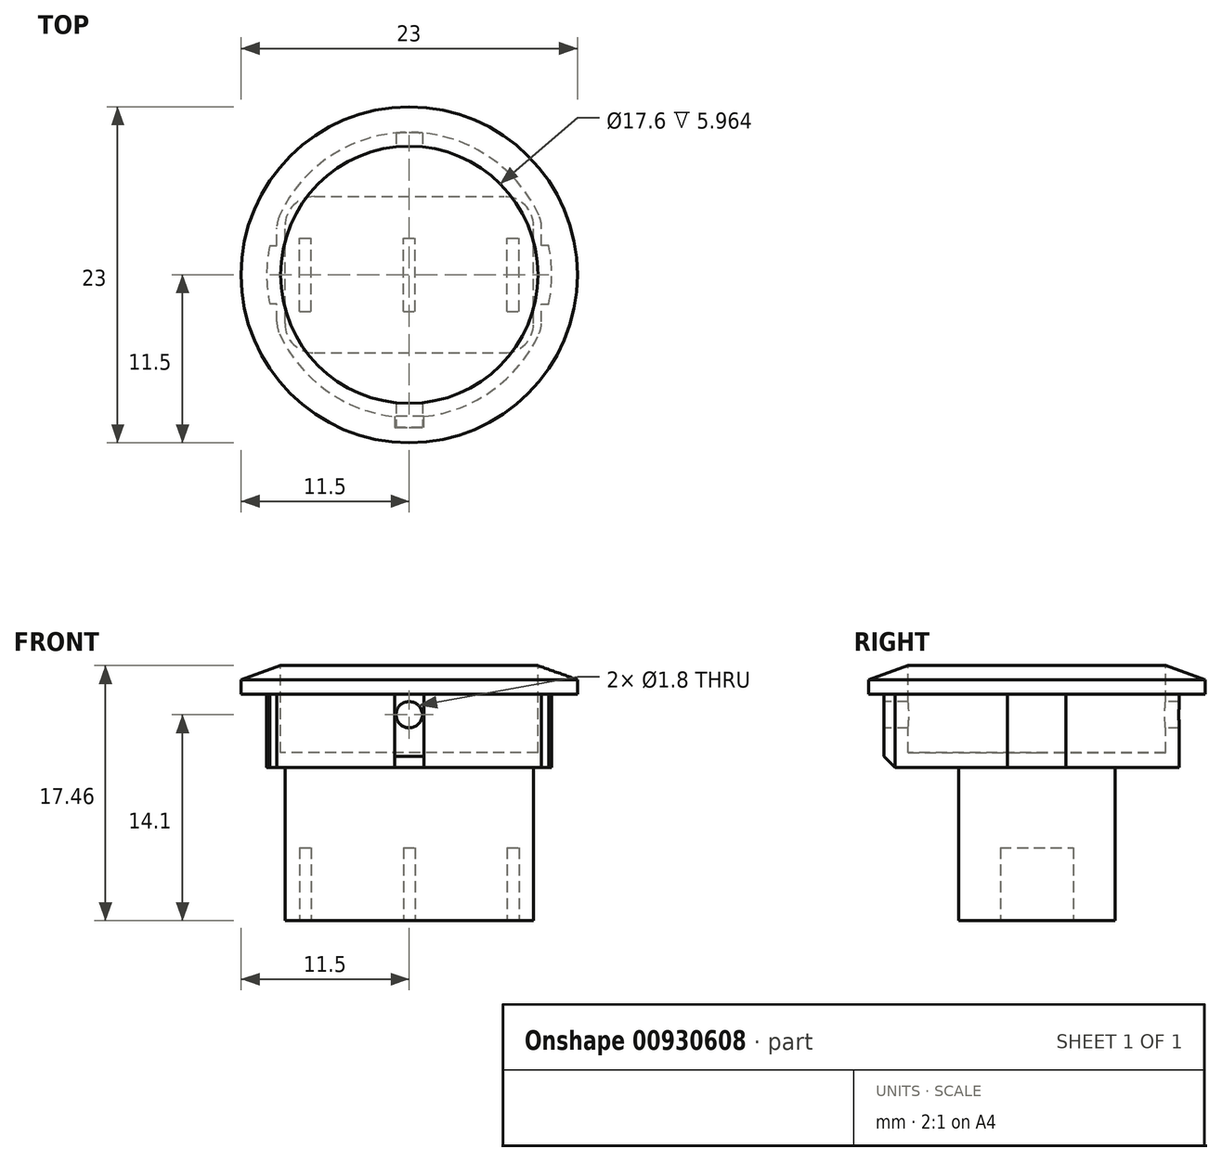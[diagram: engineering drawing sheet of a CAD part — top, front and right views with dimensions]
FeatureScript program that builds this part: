
annotation { "Feature Type Name" : "Feature", "Feature Type Description" : "" }
export const myFeature = defineFeature(function(context is Context, id is Id, definition is map)
    precondition{}
    {
        {
            var Q0;
            Q0=qCreatedBy(makeId("Top.planeOp"),FACE);
            var sketch = newSketch(context, id + "F0", { "sketchPlane" : qUnion([Q0])});
            skCircle(sketch, "E0", {"center": v(0, 0) * mm, "radius": 11.5 * mm});
            skSolve(sketch);
        }
        {
            var Q0;
            Q0=qSketchRegion(id+"F0",true);
            extrude(context, id + "F1", {"entities" : qUnion([Q0]), "depth" : 2 * mm, "offsetDistance" : 25 * mm});
        }
        {
            var Q0;
            Q0=makeQuery(id+"F1.opExtrude","CAP_FACE",FACE,{"disambiguationData":[OSD([sQuery(id+"F0.wireOp",EDGE,"E0")])],"isStart":true});
            var sketch = newSketch(context, id + "F2", { "sketchPlane" : qUnion([Q0])});
            skArc(sketch, "E1", {"start": v(-9.05, -3.63) * mm, "mid": v(0, -9.75) * mm, "end": v(9.05, -3.63) * mm});
            skLineSegment(sketch, "E2", {"start": v(-9.05, 3.63) * mm, "end": v(-9.05, -3.63) * mm});
            skLineSegment(sketch, "E3", {"start": v(9.05, 3.63) * mm, "end": v(9.05, -3.63) * mm});
            skArc(sketch, "E4.trimOffspring", {"start": v(9.05, 3.63) * mm, "mid": v(5.87, 7.78) * mm, "end": v(1, 9.7) * mm});
            skLineSegment(sketch, "E5", {"start": v(-1, 9.7) * mm, "end": v(-1, 10.45) * mm});
            skLineSegment(sketch, "E6", {"start": v(-1, 10.45) * mm, "end": v(1, 10.45) * mm});
            skLineSegment(sketch, "E7", {"start": v(1, 10.45) * mm, "end": v(1, 9.7) * mm});
            skArc(sketch, "E8.trimOffspring", {"start": v(-1, 9.7) * mm, "mid": v(-5.87, 7.78) * mm, "end": v(-9.05, 3.63) * mm});
            skLineSegment(sketch, "E9", {"start": v(-9.05, 2) * mm, "end": v(-9.54, 2) * mm});
            skLineSegment(sketch, "E10", {"start": v(-9.54, -2) * mm, "end": v(-9.05, -2) * mm});
            skLineSegment(sketch, "E11", {"start": v(9.05, 2) * mm, "end": v(9.54, 2) * mm});
            skLineSegment(sketch, "E12", {"start": v(9.54, -2) * mm, "end": v(9.05, -2) * mm});
            skArc(sketch, "E13", {"start": v(-9.05, 3.63) * mm, "mid": v(-9.33, 2.82) * mm, "end": v(-9.54, 2) * mm, "construction": true});
            skArc(sketch, "E14", {"start": v(9.05, -3.63) * mm, "mid": v(9.33, -2.82) * mm, "end": v(9.54, -2) * mm, "construction": true});
            skArc(sketch, "E15.trimOffspring", {"start": v(-9.54, -2) * mm, "mid": v(-9.33, -2.82) * mm, "end": v(-9.05, -3.63) * mm, "construction": true});
            skArc(sketch, "E16", {"start": v(-9.54, 2) * mm, "mid": v(-9.75, 0) * mm, "end": v(-9.54, -2) * mm});
            skArc(sketch, "E17.trimOffspring", {"start": v(9.54, 2) * mm, "mid": v(9.33, 2.82) * mm, "end": v(9.05, 3.63) * mm, "construction": true});
            skArc(sketch, "E18", {"start": v(9.54, -2) * mm, "mid": v(9.75, 0) * mm, "end": v(9.54, 2) * mm});
            skSolve(sketch);
        }
        {
            var Q0;
            Q0=qSketchRegion(id+"F2",true);
            extrude(context, id + "F3", {"entities" : qUnion([Q0]), "operationType" : NewBodyOperationType.ADD, "depth" : 5 * mm, "offsetDistance" : 25 * mm});
        }
        {
            var Q0;
            Q0=makeQuery(id+"F3.opExtrude","CAP_FACE",FACE,{"disambiguationData":[OSD([sQuery(id+"F2.wireOp",EDGE,"E1")])],"isStart":false});
            var sketch = newSketch(context, id + "F4", { "sketchPlane" : qUnion([Q0])});
            skLineSegment(sketch, "E19.bottom", {"start": v(-6.5, 5.35) * mm, "end": v(6.5, 5.35) * mm});
            skLineSegment(sketch, "E19.top", {"start": v(-6.5, -5.35) * mm, "end": v(6.5, -5.35) * mm});
            skLineSegment(sketch, "E19.left", {"start": v(-8.5, 3.35) * mm, "end": v(-8.5, -3.35) * mm});
            skLineSegment(sketch, "E19.right", {"start": v(8.5, 3.35) * mm, "end": v(8.5, -3.35) * mm});
            skPoint(sketch, "E20.visualSharp", {"position": v(-8.5, 5.35) * mm});
            skArc(sketch, "E20.filletArc", {"start": v(-6.5, 5.35) * mm, "mid": v(-7.91, 4.76) * mm, "end": v(-8.5, 3.35) * mm});
            skPoint(sketch, "E21.visualSharp", {"position": v(8.5, 5.35) * mm});
            skArc(sketch, "E21.filletArc", {"start": v(8.5, 3.35) * mm, "mid": v(7.91, 4.76) * mm, "end": v(6.5, 5.35) * mm});
            skPoint(sketch, "E22.visualSharp", {"position": v(8.5, -5.35) * mm});
            skArc(sketch, "E22.filletArc", {"start": v(6.5, -5.35) * mm, "mid": v(7.91, -4.76) * mm, "end": v(8.5, -3.35) * mm});
            skPoint(sketch, "E23.visualSharp", {"position": v(-8.5, -5.35) * mm});
            skArc(sketch, "E23.filletArc", {"start": v(-8.5, -3.35) * mm, "mid": v(-7.91, -4.76) * mm, "end": v(-6.5, -5.35) * mm});
            skSolve(sketch);
        }
        {
            var Q0;
            Q0=qSketchRegion(id+"F4",true);
            extrude(context, id + "F5", {"entities" : qUnion([Q0]), "operationType" : NewBodyOperationType.ADD, "depth" : 10.5 * mm, "offsetDistance" : 25 * mm});
        }
        {
            var Q0;
            Q0=makeQuery(id+"F5.opExtrude","CAP_FACE",FACE,{"disambiguationData":[OSD([sQuery(id+"F4.wireOp",EDGE,"E19.bottom"),sQuery(id+"F4.wireOp",EDGE,"E19.top"),sQuery(id+"F4.wireOp",EDGE,"E19.left"),sQuery(id+"F4.wireOp",EDGE,"E19.right"),sQuery(id+"F4.wireOp",EDGE,"E20.filletArc"),sQuery(id+"F4.wireOp",EDGE,"E21.filletArc"),sQuery(id+"F4.wireOp",EDGE,"E22.filletArc"),sQuery(id+"F4.wireOp",EDGE,"E23.filletArc")])],"isStart":false});
            var sketch = newSketch(context, id + "F6", { "sketchPlane" : qUnion([Q0])});
            skLineSegment(sketch, "E24.bottom", {"start": v(-0.4, 2.5) * mm, "end": v(0.4, 2.5) * mm});
            skLineSegment(sketch, "E24.top", {"start": v(-0.4, -2.5) * mm, "end": v(0.4, -2.5) * mm});
            skLineSegment(sketch, "E24.left", {"start": v(-0.4, 2.5) * mm, "end": v(-0.4, -2.5) * mm});
            skLineSegment(sketch, "E24.right", {"start": v(0.4, 2.5) * mm, "end": v(0.4, -2.5) * mm});
            skLineSegment(sketch, "E25.bottom", {"start": v(-7.5, 2.5) * mm, "end": v(-6.7, 2.5) * mm});
            skLineSegment(sketch, "E25.top", {"start": v(-7.5, -2.5) * mm, "end": v(-6.7, -2.5) * mm});
            skLineSegment(sketch, "E25.left", {"start": v(-7.5, 2.5) * mm, "end": v(-7.5, -2.5) * mm});
            skLineSegment(sketch, "E25.right", {"start": v(-6.7, 2.5) * mm, "end": v(-6.7, -2.5) * mm});
            skLineSegment(sketch, "E26.bottom", {"start": v(6.7, 2.5) * mm, "end": v(7.5, 2.5) * mm});
            skLineSegment(sketch, "E26.top", {"start": v(6.7, -2.5) * mm, "end": v(7.5, -2.5) * mm});
            skLineSegment(sketch, "E26.left", {"start": v(6.7, 2.5) * mm, "end": v(6.7, -2.5) * mm});
            skLineSegment(sketch, "E26.right", {"start": v(7.5, 2.5) * mm, "end": v(7.5, -2.5) * mm});
            skSolve(sketch);
        }
        {
            var Q0;
            Q0=qSketchRegion(id+"F6",true);
            extrude(context, id + "F7", {"entities" : qUnion([Q0]), "operationType" : NewBodyOperationType.REMOVE, "oppositeDirection" : true, "depth" : 5 * mm, "offsetDistance" : 25 * mm});
        }
        {
            var Q0;
            Q0=makeQuery(id+"F1.opExtrude","CAP_FACE",FACE,{"disambiguationData":[OSD([sQuery(id+"F0.wireOp",EDGE,"E0")])],"isStart":false});
            var sketch = newSketch(context, id + "F8", { "sketchPlane" : qUnion([Q0])});
            skCircle(sketch, "E27", {"center": v(0, 0) * mm, "radius": 8.8 * mm});
            skSolve(sketch);
        }
        {
            var Q0;
            Q0=qSketchRegion(id+"F8",true);
            extrude(context, id + "F9", {"entities" : qUnion([Q0]), "operationType" : NewBodyOperationType.REMOVE, "oppositeDirection" : true, "depth" : 6 * mm, "offsetDistance" : 25 * mm});
        }
        {
            var Q0;
            Q0=makeQuery(id+"F1.opExtrude","CAP_EDGE",EDGE,{"disambiguationData":[OSD([sQuery(id+"F0.wireOp",EDGE,"E0")])],"isStart":false});
            chamfer(context, id + "F10", {"entities" : qUnion([Q0]), "chamferType" : ChamferType.TWO_OFFSETS, "width1" : 2.8 * mm, "oppositeDirection" : false, "width2" : 1 * mm, "tangentPropagation" : true});
        }
        {
            var Q0;
            Q0=makeQuery(id+"F3.opExtrude","SWEPT_EDGE",EDGE,{"disambiguationData":[OSD([sQuery(id+"F2.wireOp",EDGE,"E1"),sQuery(id+"F2.wireOp",EDGE,"E2")])]});
            var Q1;
            Q1=makeQuery(id+"F3.opExtrude","SWEPT_EDGE",EDGE,{"disambiguationData":[OSD([sQuery(id+"F2.wireOp",EDGE,"E2"),sQuery(id+"F2.wireOp",EDGE,"E8.trimOffspring")])]});
            var Q2;
            Q2=makeQuery(id+"F3.opExtrude","SWEPT_EDGE",EDGE,{"disambiguationData":[OSD([sQuery(id+"F2.wireOp",EDGE,"E3"),sQuery(id+"F2.wireOp",EDGE,"E4.trimOffspring")])]});
            var Q3;
            Q3=makeQuery(id+"F3.opExtrude","SWEPT_EDGE",EDGE,{"disambiguationData":[OSD([sQuery(id+"F2.wireOp",EDGE,"E1"),sQuery(id+"F2.wireOp",EDGE,"E3")])]});
            fillet(context, id + "F11", {"entities" : qUnion([Q0, Q1, Q2, Q3]), "radius" : 2 * mm, "tangentPropagation" : true, "allowEdgeOverflow" : false});
        }
        {
            var Q0;
            Q0=makeQuery(id+"F3.opExtrude","CAP_EDGE",EDGE,{"disambiguationData":[OSD([sQuery(id+"F2.wireOp",EDGE,"E6")])],"isStart":false});
            chamfer(context, id + "F12", {"entities" : qUnion([Q0]), "width" : 0.75 * mm, "tangentPropagation" : true});
        }
        {
            var Q0;
            Q0=makeQuery(id+"F3.opExtrude","SWEPT_FACE",FACE,{"disambiguationData":[OSD([sQuery(id+"F2.wireOp",EDGE,"E6")])]});
            var sketch = newSketch(context, id + "F13", { "sketchPlane" : qUnion([Q0])});
            skCircle(sketch, "E28", {"center": v(0, -1.4) * mm, "radius": 0.9 * mm});
            skSolve(sketch);
        }
        {
            var Q0;
            Q0=qSketchRegion(id+"F13",true);
            var Q1;
            Q1=makeQuery(id+"F3.opExtrude","SWEPT_FACE",FACE,{"disambiguationData":[OSD([sQuery(id+"F2.wireOp",EDGE,"E1")])]});
            extrude(context, id + "F14", {"entities" : qUnion([Q0]), "operationType" : NewBodyOperationType.REMOVE, "endBound" : BoundingType.THROUGH_ALL, "oppositeDirection" : true, "depth" : 25 * mm, "endBoundEntityFace" : qUnion([Q1]), "offsetDistance" : 25 * mm});
        }
    });
